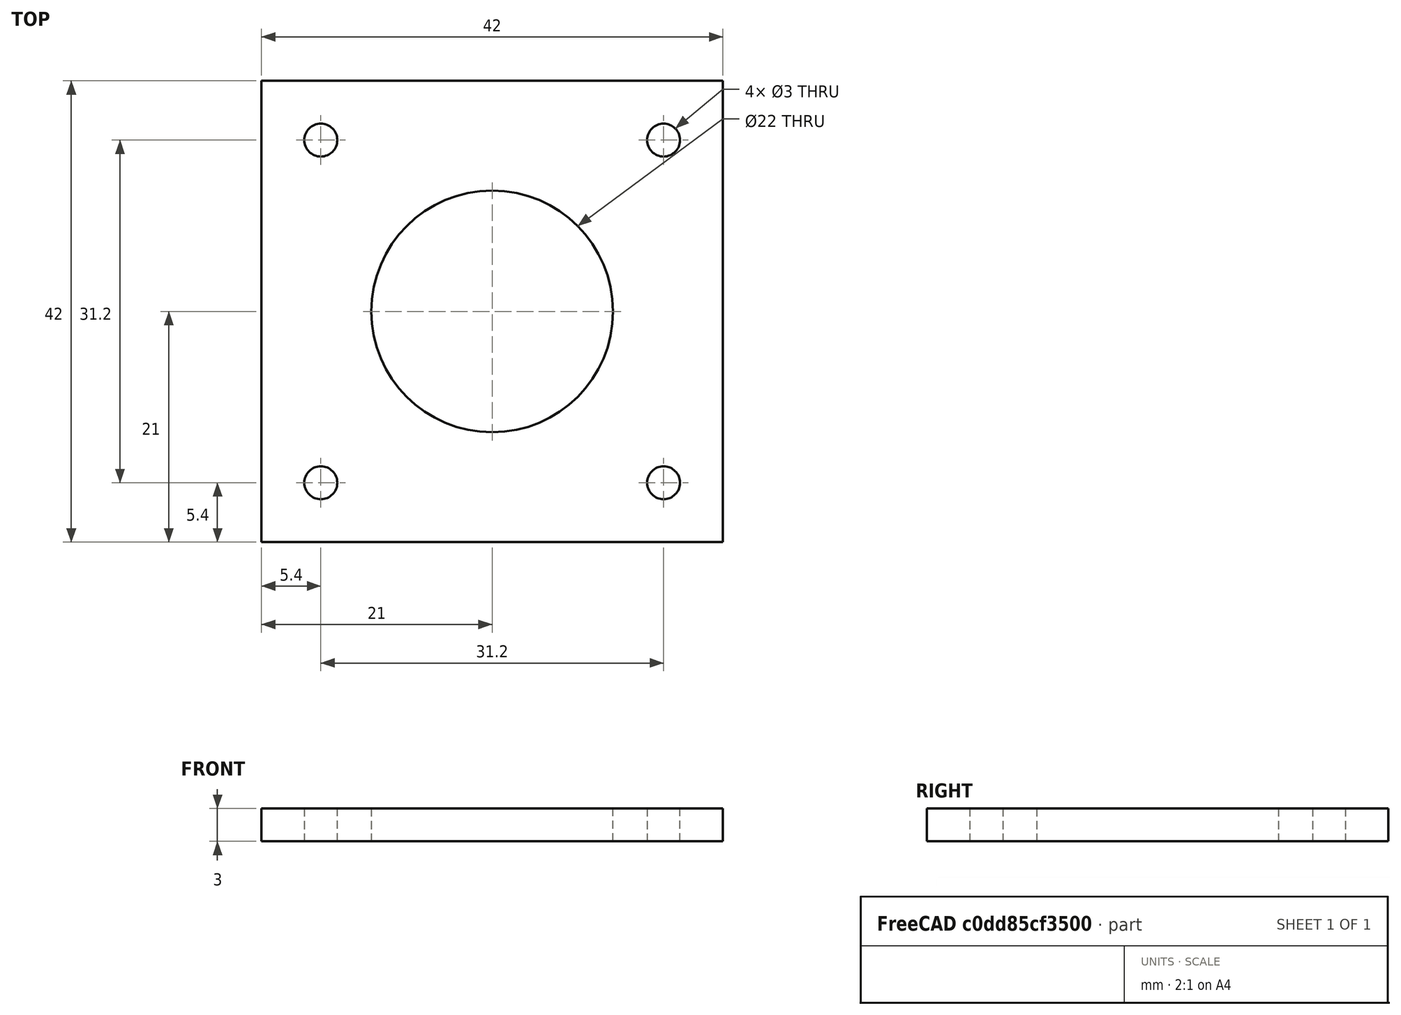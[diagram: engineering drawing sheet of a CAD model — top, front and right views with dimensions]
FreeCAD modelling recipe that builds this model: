
FCSTD DOCUMENT
Label: 4202MotorMount
objects: Sketcher::SketchObject×1, PartDesign::Pad×1
note: 3 computed .brp shape members not serialized (recipe doc carries the construction recipe); baked Part::Feature solids carry a one-line shape summary decoded from their .brp

FEATURE [Sketcher::SketchObject] Sketch
  sketch-geometry (9):
    g0: Circle CenterX=0 CenterY=0 CenterZ=0 NormalX=0 NormalY=0 NormalZ=1 Radius=11
    g1: Circle CenterX=15.6 CenterY=15.6 CenterZ=0 NormalX=0 NormalY=0 NormalZ=1 Radius=1.5
    g2: Circle CenterX=15.6 CenterY=-15.6 CenterZ=0 NormalX=0 NormalY=0 NormalZ=1 Radius=1.5
    g3: Circle CenterX=-15.6 CenterY=-15.6 CenterZ=0 NormalX=0 NormalY=0 NormalZ=1 Radius=1.5
    g4: Circle CenterX=-15.6 CenterY=15.6 CenterZ=0 NormalX=0 NormalY=0 NormalZ=1 Radius=1.5
    g5: LineSegment StartX=-21 StartY=21 StartZ=0 EndX=21 EndY=21 EndZ=0
    g6: LineSegment StartX=21 StartY=21 StartZ=0 EndX=21 EndY=-21 EndZ=0
    g7: LineSegment StartX=21 StartY=-21 StartZ=0 EndX=-21 EndY=-21 EndZ=0
    g8: LineSegment StartX=-21 StartY=-21 StartZ=0 EndX=-21 EndY=21 EndZ=0
  constraints (27):
    c: Radius(g0) = 11
    c: DistanceX(g1) = 15.6
    c: DistanceY(g1) = 15.6
    c: Radius(g1) = 1.5
    c: DistanceX(g2) = 15.6
    c: DistanceY(g2) = -15.6
    c: Radius(g2) = 1.5
    c: DistanceX(g3) = -15.6
    c: DistanceY(g3) = -15.6
    c: Radius(g3) = 1.5
    c: DistanceX(g4) = -15.6
    c: DistanceY(g4) = 15.6
    c: Radius(g4) = 1.5
    c: DistanceX(g0) = 0
    c: DistanceY(g0) = 0
    c: Coincident(g5,g6)
    c: Coincident(g6,g7)
    c: Coincident(g7,g8)
    c: Coincident(g8,g5)
    c: Horizontal(g5)
    c: Horizontal(g7)
    c: Vertical(g6)
    c: Vertical(g8)
    c: DistanceX(g7) = -42
    c: DistanceY(g8) = 42
    c: DistanceX(g5) = 21
    c: DistanceY(g5) = 21
FEATURE [PartDesign::Pad] Pad
  Length = 3
  MirroredExtent = false
  Sketch = -> Sketch
